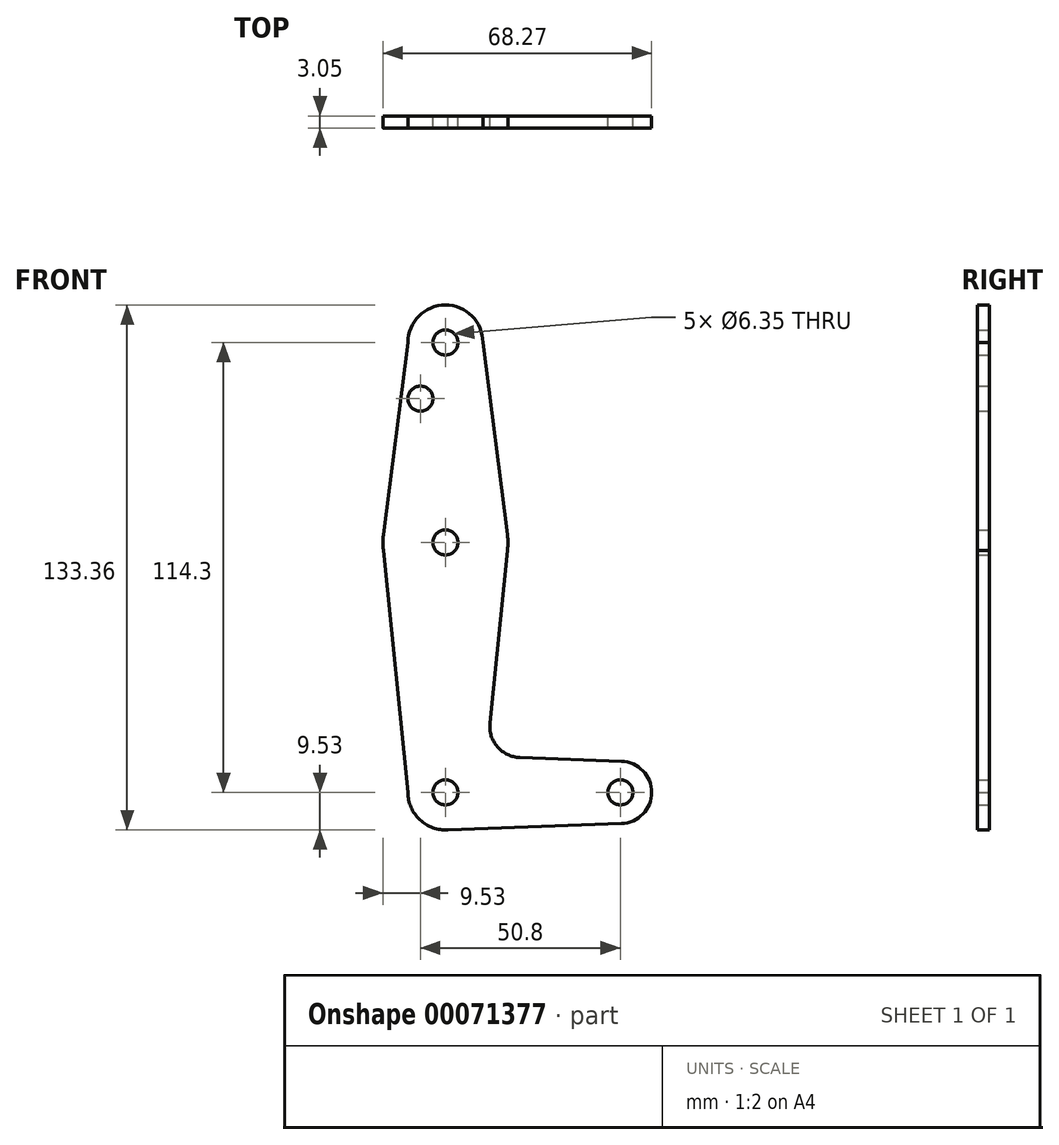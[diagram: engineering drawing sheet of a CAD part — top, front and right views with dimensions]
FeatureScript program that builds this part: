
annotation { "Feature Type Name" : "Feature", "Feature Type Description" : "" }
export const myFeature = defineFeature(function(context is Context, id is Id, definition is map)
    precondition{}
    {
        {
            var Q0;
            Q0=qCreatedBy(makeId("Front.planeOp"),FACE);
            var sketch = newSketch(context, id + "F0", { "sketchPlane" : qUnion([Q0])});
            skCircle(sketch, "E0", {"center": v(0, 0) * mm, "radius": 9.53 * mm});
            skCircle(sketch, "E1", {"center": v(0, 63.5) * mm, "radius": 15.88 * mm});
            skCircle(sketch, "E2", {"center": v(0, 114.3) * mm, "radius": 9.53 * mm});
            skCircle(sketch, "E3", {"center": v(44.45, 0) * mm, "radius": 7.94 * mm});
            skLineSegment(sketch, "E4", {"start": v(0, 114.3) * mm, "end": v(0, 0) * mm, "construction": true});
            skLineSegment(sketch, "E5", {"start": v(44.45, 0) * mm, "end": v(0, 0) * mm, "construction": true});
            skLineSegment(sketch, "E6", {"start": v(-9.53, 114.3) * mm, "end": v(-15.75, 65.5) * mm});
            skLineSegment(sketch, "E7", {"start": v(9.53, 114.3) * mm, "end": v(15.75, 65.5) * mm});
            skLineSegment(sketch, "E8", {"start": v(-15.74, 61.4) * mm, "end": v(-9.52, 0) * mm});
            skLineSegment(sketch, "E9", {"start": v(11.3, 17.6) * mm, "end": v(15.75, 61.5) * mm});
            skLineSegment(sketch, "E10", {"start": v(18.93, 8.85) * mm, "end": v(44.73, 7.93) * mm});
            skLineSegment(sketch, "E11", {"start": v(0, -9.53) * mm, "end": v(44.73, -7.93) * mm});
            skCircle(sketch, "E12", {"center": v(-6.35, 100.03) * mm, "radius": 3.18 * mm});
            skCircle(sketch, "E13", {"center": v(0, 114.3) * mm, "radius": 3.18 * mm});
            skCircle(sketch, "E14", {"center": v(0, 63.5) * mm, "radius": 3.18 * mm});
            skCircle(sketch, "E15", {"center": v(0, 0) * mm, "radius": 3.18 * mm});
            skCircle(sketch, "E16", {"center": v(44.45, 0) * mm, "radius": 3.18 * mm});
            skPoint(sketch, "E17.newPointB", {"position": v(0, 9.53) * mm});
            skArc(sketch, "E17.filletArc", {"start": v(11.3, 17.6) * mm, "mid": v(13.22, 11.57) * mm, "end": v(18.93, 8.85) * mm});
            skSolve(sketch);
        }
        {
            var Q0;
            Q0 = qSketchRegion(id + "F0", true);
            extrude(context, id + "F1", {"entities" : qUnion([Q0]), "depth" : 3.05 * mm});
        }
        {
            var Q0;
            Q0 = qSketchRegion(id + "F0", true);
            extrude(context, id + "F2", {"entities" : qUnion([Q0]), "operationType" : NewBodyOperationType.ADD, "depth" : 3.05 * mm});
        }
    });
